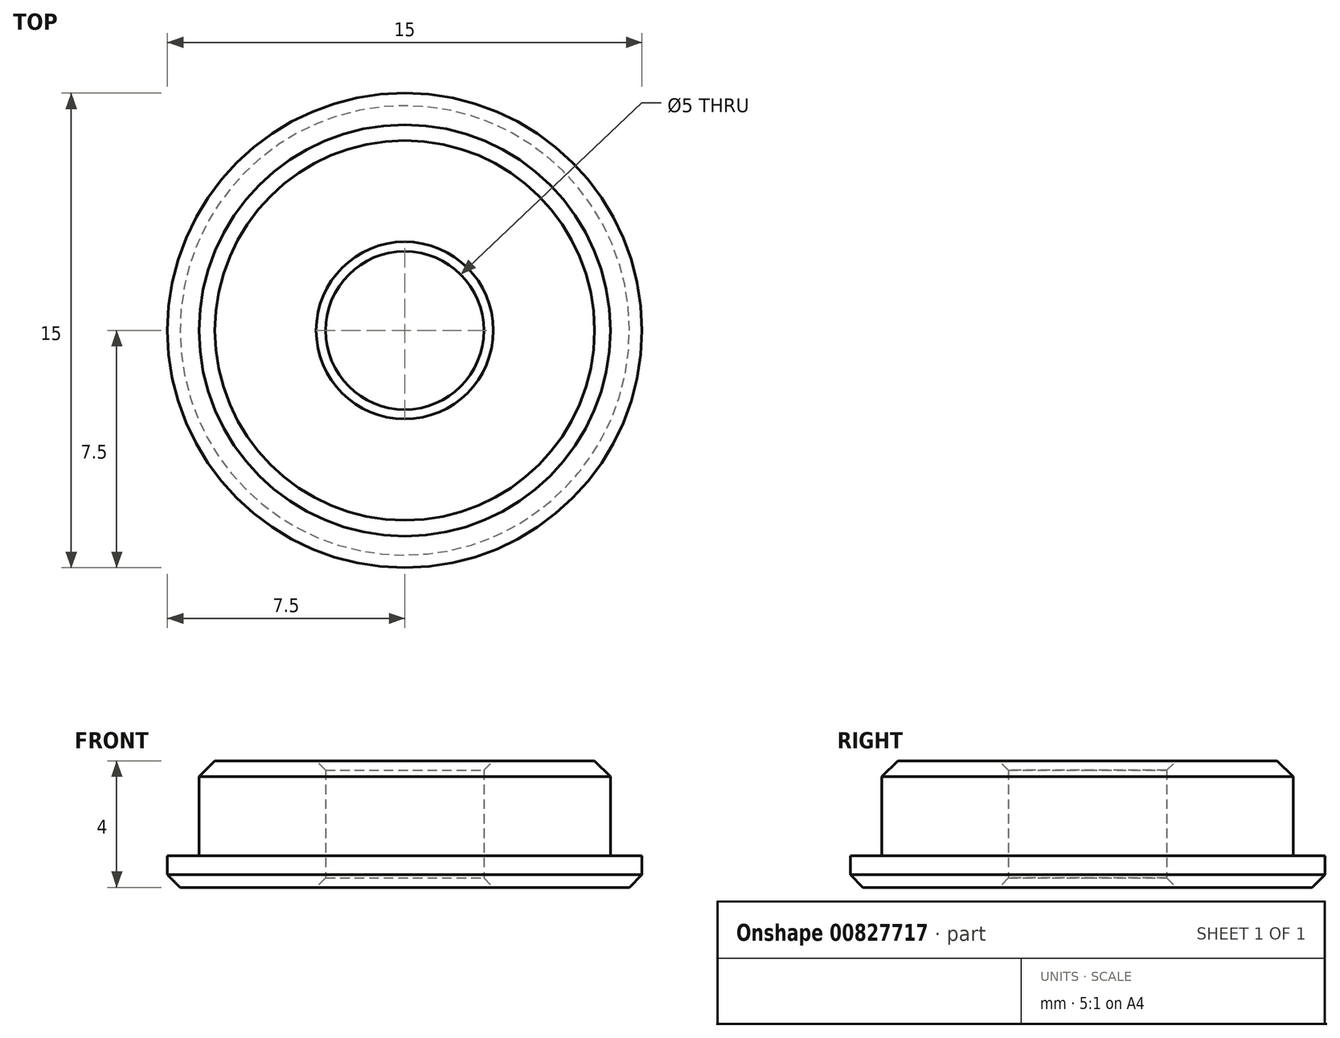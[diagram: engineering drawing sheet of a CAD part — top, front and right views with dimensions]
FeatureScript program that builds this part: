
annotation { "Feature Type Name" : "Feature", "Feature Type Description" : "" }
export const myFeature = defineFeature(function(context is Context, id is Id, definition is map)
    precondition{}
    {
        {
            var Q0;
            Q0=qCreatedBy(makeId("Front.planeOp"),FACE);
            var sketch = newSketch(context, id + "F0", { "sketchPlane" : qUnion([Q0])});
            skLineSegment(sketch, "E0", {"start": v(0, 0) * mm, "end": v(0, 20.88) * mm});
            skLineSegment(sketch, "E1", {"start": v(7.5, 0) * mm, "end": v(7.5, 1) * mm});
            skLineSegment(sketch, "E2", {"start": v(7.5, 1) * mm, "end": v(6.5, 1) * mm});
            skLineSegment(sketch, "E3", {"start": v(6.5, 1) * mm, "end": v(6.5, 4) * mm});
            skLineSegment(sketch, "E4", {"start": v(2.5, 4) * mm, "end": v(6.5, 4) * mm});
            skLineSegment(sketch, "E5", {"start": v(2.5, 4) * mm, "end": v(2.5, 0) * mm});
            skLineSegment(sketch, "E6", {"start": v(2.5, 0) * mm, "end": v(7.5, 0) * mm});
            skSolve(sketch);
        }
        {
            var Q0;
            Q0 = qSketchRegion(id + "F0", true);
            var Q1;
            Q1=sQuery(id+"F0.wireOp",EDGE,"E0");
            revolve(context, id + "F1", {"surfaceOperationType" : NewSurfaceOperationType.NEW, "entities" : qUnion([Q0]), "axis" : qUnion([Q1]), "revolveType" : RevolveType.FULL});
        }
        {
            var Q0;
            Q0=makeQuery(id+"F1.opRevolve","SWEPT_EDGE",EDGE,{"disambiguationData":[OSD([sQuery(id+"F0.wireOp",EDGE,"E3"),sQuery(id+"F0.wireOp",EDGE,"E4")])]});
            chamfer(context, id + "F2", {"entities" : qUnion([Q0]), "width" : 0.5 * mm, "tangentPropagation" : true});
        }
        {
            var Q0;
            Q0=makeQuery(id+"F1.opRevolve","SWEPT_EDGE",EDGE,{"disambiguationData":[OSD([sQuery(id+"F0.wireOp",EDGE,"E1"),sQuery(id+"F0.wireOp",EDGE,"E6")])]});
            chamfer(context, id + "F3", {"entities" : qUnion([Q0]), "width" : 0.4 * mm, "tangentPropagation" : true});
        }
        {
            var Q0;
            Q0=makeQuery(id+"F1.opRevolve","SWEPT_EDGE",EDGE,{"disambiguationData":[OSD([sQuery(id+"F0.wireOp",EDGE,"E5"),sQuery(id+"F0.wireOp",EDGE,"E6")])]});
            var Q1;
            Q1=makeQuery(id+"F1.opRevolve","SWEPT_EDGE",EDGE,{"disambiguationData":[OSD([sQuery(id+"F0.wireOp",EDGE,"E4"),sQuery(id+"F0.wireOp",EDGE,"E5")])]});
            chamfer(context, id + "F4", {"entities" : qUnion([Q0, Q1]), "width" : 0.3 * mm, "tangentPropagation" : true});
        }
    });
